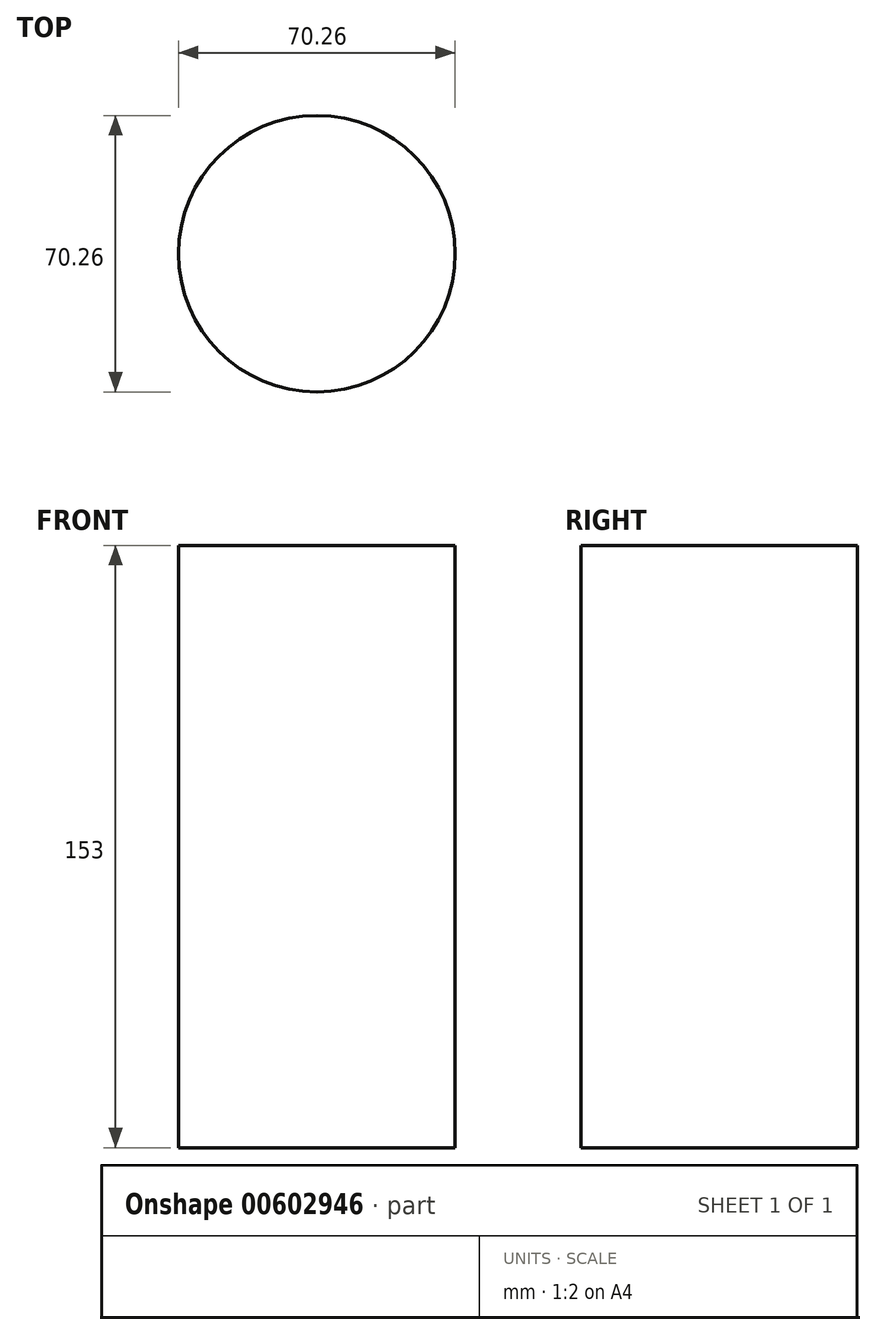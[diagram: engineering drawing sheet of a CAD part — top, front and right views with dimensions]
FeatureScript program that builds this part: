
annotation { "Feature Type Name" : "Feature", "Feature Type Description" : "" }
export const myFeature = defineFeature(function(context is Context, id is Id, definition is map)
    precondition{}
    {
        {
            var Q0;
            Q0=qCreatedBy(makeId("Top.planeOp"),FACE);
            var sketch = newSketch(context, id + "F0", { "sketchPlane" : qUnion([Q0])});
            skCircle(sketch, "E0", {"center": v(0, 0) * mm, "radius": 35.13 * mm});
            skSolve(sketch);
        }
        {
            var Q0;
            Q0 = qSketchRegion(id + "F0", true);
            extrude(context, id + "F1", {"entities" : qUnion([Q0]), "depth" : 58 * mm, "offsetDistance" : 25 * mm});
        }
        {
            var Q0;
            Q0=makeQuery(id+"F1.opExtrude","CAP_FACE",FACE,{"disambiguationData":[OSD([sQuery(id+"F0.wireOp",EDGE,"E0")])],"isStart":true});
            extrude(context, id + "F2", {"entities" : qUnion([Q0]), "operationType" : NewBodyOperationType.ADD, "depth" : 95 * mm, "offsetDistance" : 25 * mm});
        }
    });
